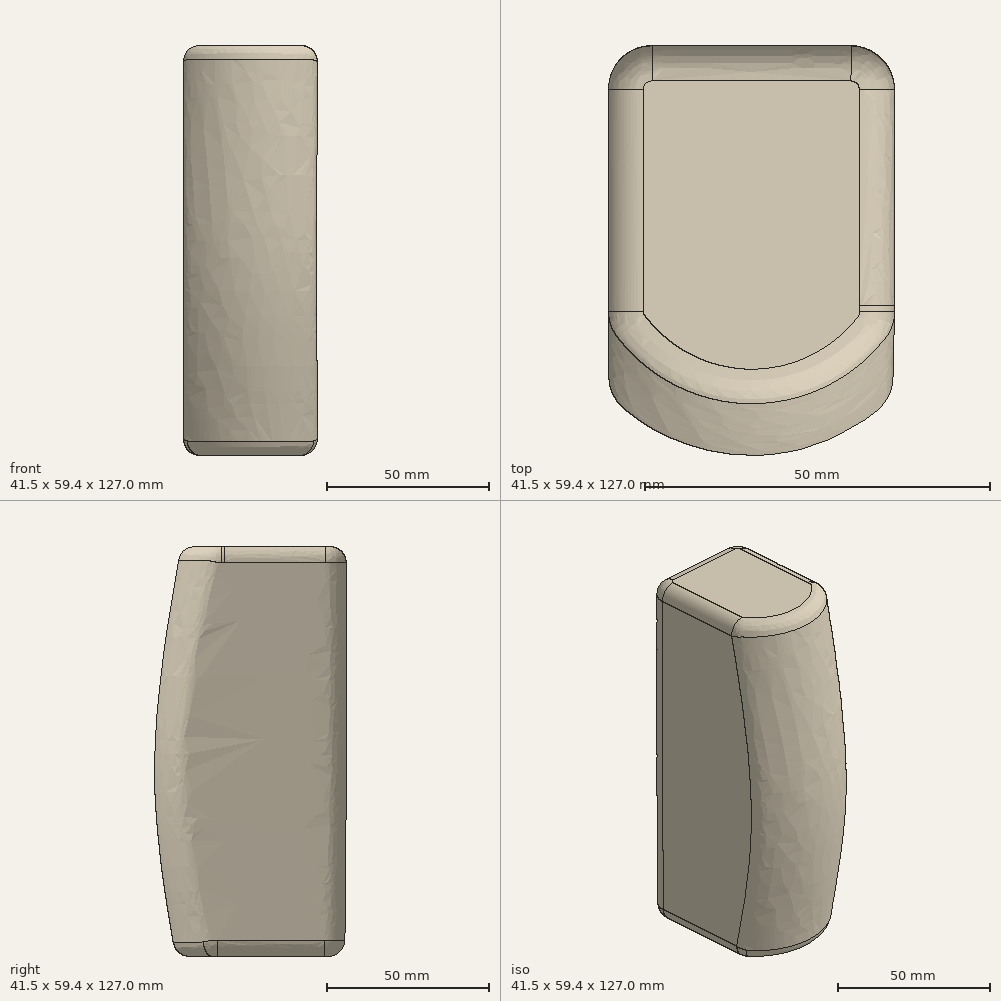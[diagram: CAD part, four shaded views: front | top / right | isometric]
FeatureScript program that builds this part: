
annotation { "Feature Type Name" : "Feature", "Feature Type Description" : "" }
export const myFeature = defineFeature(function(context is Context, id is Id, definition is map)
    precondition{}
    {
        {
            var Q0;
            Q0=qCreatedBy(makeId("Top.planeOp"),FACE);
            cPlane(context, id + "F0", {"entities" : qUnion([Q0]), "cplaneType" : CPlaneType.OFFSET, "offset" : 127 * mm, "width" : 152.4 * mm, "height" : 152.4 * mm});
        }
        {
            var Q0;
            Q0=qCreatedBy(makeId("Top.planeOp"),FACE);
            cPlane(context, id + "F1", {"entities" : qUnion([Q0]), "cplaneType" : CPlaneType.OFFSET, "offset" : 50.8 * mm, "width" : 152.4 * mm, "height" : 152.4 * mm});
        }
        {
            var Q0;
            Q0=qCreatedBy(makeId("Top.planeOp"),FACE);
            var sketch = newSketch(context, id + "F2", { "sketchPlane" : qUnion([Q0])});
            skLineSegment(sketch, "E0", {"start": v(-12.75, 33.62) * mm, "end": v(16.03, 33.62) * mm});
            skLineSegment(sketch, "E1", {"start": v(-19.1, 27.27) * mm, "end": v(-19.1, -5.73) * mm});
            skLineSegment(sketch, "E2", {"start": v(22.38, 27.27) * mm, "end": v(22.38, -5.73) * mm});
            skArc(sketch, "E3", {"start": v(-17.61, -9.82) * mm, "mid": v(1.64, -18.78) * mm, "end": v(20.89, -9.82) * mm});
            skPoint(sketch, "E4.visualSharp", {"position": v(-19.1, 33.62) * mm});
            skArc(sketch, "E4.filletArc", {"start": v(-12.75, 33.62) * mm, "mid": v(-17.24, 31.76) * mm, "end": v(-19.1, 27.27) * mm});
            skPoint(sketch, "E5.visualSharp", {"position": v(22.38, 33.62) * mm});
            skArc(sketch, "E5.filletArc", {"start": v(22.38, 27.27) * mm, "mid": v(20.52, 31.76) * mm, "end": v(16.03, 33.62) * mm});
            skPoint(sketch, "E6.visualSharp", {"position": v(22.38, -7.86) * mm});
            skArc(sketch, "E6.filletArc", {"start": v(20.89, -9.82) * mm, "mid": v(22, -7.9) * mm, "end": v(22.38, -5.73) * mm});
            skPoint(sketch, "E7.visualSharp", {"position": v(-19.1, -7.86) * mm});
            skArc(sketch, "E7.filletArc", {"start": v(-19.1, -5.73) * mm, "mid": v(-18.72, -7.9) * mm, "end": v(-17.61, -9.82) * mm});
            skSolve(sketch);
        }
        {
            var Q0;
            Q0=qCreatedBy(id+"F0.planeOp",FACE);
            var sketch = newSketch(context, id + "F3", { "sketchPlane" : qUnion([Q0])});
            skLineSegment(sketch, "E8", {"start": v(-12.75, 34.06) * mm, "end": v(16.03, 34.06) * mm});
            skLineSegment(sketch, "E9", {"start": v(22.38, 27.7) * mm, "end": v(22.38, -3.52) * mm});
            skLineSegment(sketch, "E10", {"start": v(-19.1, 27.7) * mm, "end": v(-19.1, -3.34) * mm});
            skArc(sketch, "E11", {"start": v(-17.88, -7.08) * mm, "mid": v(1.55, -17.05) * mm, "end": v(21.11, -7.32) * mm});
            skPoint(sketch, "E12.visualSharp", {"position": v(22.38, 34.06) * mm});
            skArc(sketch, "E12.filletArc", {"start": v(22.38, 27.7) * mm, "mid": v(20.52, 32.2) * mm, "end": v(16.03, 34.06) * mm});
            skPoint(sketch, "E13.visualSharp", {"position": v(-19.1, 34.06) * mm});
            skArc(sketch, "E13.filletArc", {"start": v(-12.75, 34.06) * mm, "mid": v(-17.24, 32.2) * mm, "end": v(-19.1, 27.7) * mm});
            skPoint(sketch, "E14.visualSharp", {"position": v(-19.1, -5.24) * mm});
            skArc(sketch, "E14.filletArc", {"start": v(-19.1, -3.34) * mm, "mid": v(-18.79, -5.3) * mm, "end": v(-17.88, -7.08) * mm});
            skPoint(sketch, "E15.visualSharp", {"position": v(22.38, -5.46) * mm});
            skArc(sketch, "E15.filletArc", {"start": v(21.11, -7.32) * mm, "mid": v(22.05, -5.52) * mm, "end": v(22.38, -3.52) * mm});
            skSolve(sketch);
        }
        {
            var Q0;
            Q0=qCreatedBy(id+"F1.planeOp",FACE);
            var sketch = newSketch(context, id + "F4", { "sketchPlane" : qUnion([Q0])});
            skLineSegment(sketch, "E16", {"start": v(-12.75, 34.06) * mm, "end": v(15.8, 34.06) * mm});
            skLineSegment(sketch, "E17", {"start": v(22.16, 27.7) * mm, "end": v(22.16, -13.8) * mm});
            skLineSegment(sketch, "E18", {"start": v(-19.1, 27.7) * mm, "end": v(-19.1, -13.57) * mm});
            skPoint(sketch, "E19.visualSharp", {"position": v(-19.1, 34.06) * mm});
            skArc(sketch, "E19.filletArc", {"start": v(-12.75, 34.06) * mm, "mid": v(-17.24, 32.2) * mm, "end": v(-19.1, 27.7) * mm});
            skPoint(sketch, "E20.visualSharp", {"position": v(22.16, 34.06) * mm});
            skArc(sketch, "E20.filletArc", {"start": v(22.16, 27.7) * mm, "mid": v(20.3, 32.2) * mm, "end": v(15.8, 34.06) * mm});
            skArc(sketch, "E21", {"start": v(-16.85, -18.42) * mm, "mid": v(1.44, -25.2) * mm, "end": v(19.83, -18.71) * mm});
            skPoint(sketch, "E22.visualSharp", {"position": v(-19.1, -16.3) * mm});
            skArc(sketch, "E22.filletArc", {"start": v(-19.1, -13.57) * mm, "mid": v(-18.51, -16.24) * mm, "end": v(-16.85, -18.42) * mm});
            skPoint(sketch, "E23.visualSharp", {"position": v(22.16, -16.58) * mm});
            skArc(sketch, "E23.filletArc", {"start": v(19.83, -18.71) * mm, "mid": v(21.55, -16.52) * mm, "end": v(22.16, -13.8) * mm});
            skSolve(sketch);
        }
        {
            var Q0;
            Q0 = qSketchRegion(id + "F2", true);
            var Q1;
            Q1 = qSketchRegion(id + "F4", true);
            var Q2;
            Q2 = qSketchRegion(id + "F3", true);
            loft(context, id + "F5", {"sheetProfilesArray" : [{ "sheetProfileEntities" : qUnion([Q0]) }, { "sheetProfileEntities" : qUnion([Q1]) }, { "sheetProfileEntities" : qUnion([Q2]) }]});
        }
        {
            var Q0;
            Q0=makeQuery(id+"F5.opLoft","MID_CAP_EDGE",EDGE,{"disambiguationData":[OSD([sQuery(id+"F3.wireOp",EDGE,"E8"),sQuery(id+"F3.wireOp",EDGE,"E12.filletArc"),sQuery(id+"F3.wireOp",EDGE,"E13.filletArc")])],"capPos":2.0});
            var Q1;
            Q1=makeQuery(id+"F5.opLoft","MID_CAP_EDGE",EDGE,{"disambiguationData":[OSD([sQuery(id+"F2.wireOp",EDGE,"E0"),sQuery(id+"F2.wireOp",EDGE,"E4.filletArc"),sQuery(id+"F2.wireOp",EDGE,"E5.filletArc")])],"capPos":0.0});
            fillet(context, id + "F6", {"entities" : qUnion([Q0, Q1]), "radius" : 5.08 * mm, "tangentPropagation" : true, "allowEdgeOverflow" : false});
        }
    });
